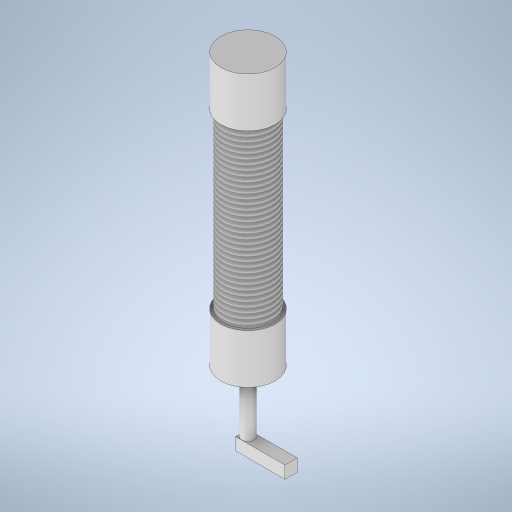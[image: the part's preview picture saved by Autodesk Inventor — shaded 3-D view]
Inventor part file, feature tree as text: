
AUTODESK INVENTOR PART (.ipt)
format: ipt  version: 2023 (Build 270158000, 158)  size: 294,400 bytes
history: native  units: mm
features: sketch x6, extrude x5, other x1, thread x1
ambient origin geometry x8: Origin, YZ Plane, XZ Plane, XY Plane, X Axis, Y Axis, Z Axis, Center Point
bodies: Body1 (feature_tree)
feature tree (13):
  other  "Твердое тело1"
  extrude  "Выдавливание1"  Depth=20.0mm
  thread  "Резьба2"
  sketch  "Эскиз2"
  extrude  "Выдавливание2"  Depth=70.0mm TaperAngle=0.0deg
  extrude  "Выдавливание5"  Depth=70.0mm TaperAngle=0.0deg
  extrude  "Выдавливание6"  Depth=22.0mm
  extrude  "Выдавливание7"  Depth=20.0mm TaperAngle=0.0deg
  sketch  "Эскиз1"
  sketch  "Эскиз3"
  sketch  "Эскиз6"
  sketch  "Эскиз7"
  sketch  "Эскиз8"
